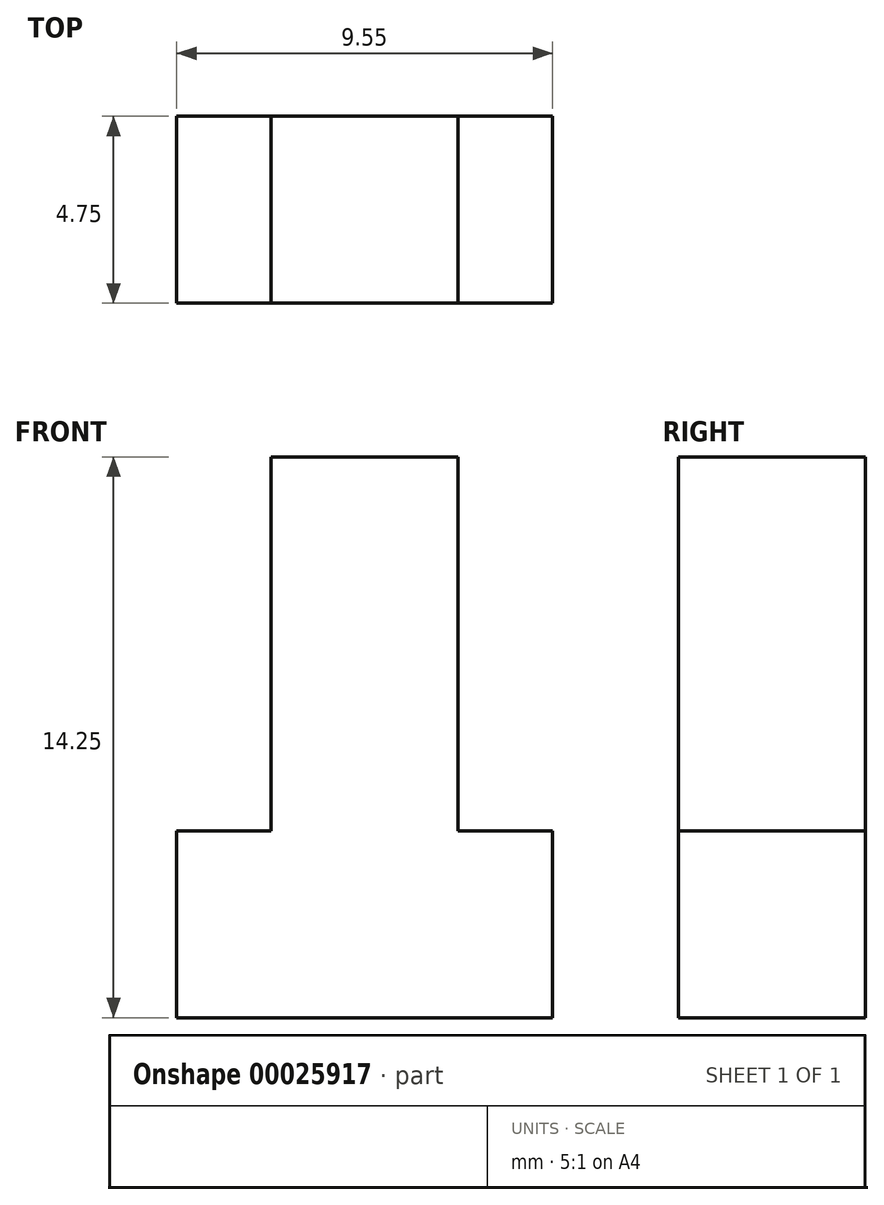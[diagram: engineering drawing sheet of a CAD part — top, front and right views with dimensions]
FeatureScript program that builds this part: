
annotation { "Feature Type Name" : "Feature", "Feature Type Description" : "" }
export const myFeature = defineFeature(function(context is Context, id is Id, definition is map)
    precondition{}
    {
        {
            var Q0;
            Q0=qCreatedBy(makeId("Front.planeOp"),FACE);
            var sketch = newSketch(context, id + "F0", { "sketchPlane" : qUnion([Q0])});
            skLineSegment(sketch, "E0", {"start": v(0, 0) * mm, "end": v(9.55, 0) * mm});
            skLineSegment(sketch, "E1", {"start": v(9.55, 0) * mm, "end": v(9.55, 4.75) * mm});
            skLineSegment(sketch, "E2", {"start": v(9.55, 4.75) * mm, "end": v(7.15, 4.75) * mm});
            skLineSegment(sketch, "E3", {"start": v(7.15, 4.75) * mm, "end": v(7.15, 14.25) * mm});
            skLineSegment(sketch, "E4", {"start": v(7.15, 14.25) * mm, "end": v(2.4, 14.25) * mm});
            skLineSegment(sketch, "E5", {"start": v(2.4, 14.25) * mm, "end": v(2.4, 4.75) * mm});
            skLineSegment(sketch, "E6", {"start": v(2.4, 4.75) * mm, "end": v(0, 4.75) * mm});
            skLineSegment(sketch, "E7", {"start": v(0, 4.75) * mm, "end": v(0, 0) * mm});
            skSolve(sketch);
        }
        {
            var Q0;
            Q0=makeQuery(id+"F0.imprint","IMPRINT",FACE,{"disambiguationData":[TD([[makeQuery(id+"F0.imprint","IMPRINT",EDGE,{"derivedFrom":sQuery(id+"F0.wireOp",EDGE,"E0")}),1.0]])]});
            extrude(context, id + "F1", {"entities" : qUnion([Q0]), "depth" : 4.75 * mm});
        }
    });
